# Revit family: STL23717_30 - 10°
name_source: partatom
category: Luminárias
units: mm (PartAtom-declared; Revit-internal decimal feet)

## family parameters
Com base no plano de trabalho = Não
Compartilhado = Não
Corte com vazios quando carregada = Não
Cota do conector redondo = Utilizar diâmetro
Fonte luminosa = Sim
Manter orientação da anotação = Não
Ponto de cálculo do ambiente = Não
Sempre na vertical = Sim
Tipo de parte = Normal

## types (1)
- STL23717/30 - BIVOLT - 3000K - 360lm - 14°
    Altura da Caixa de Instalação = 0.14 m
    Altura do Embutido = 0.1 m
    Arquivo de rede fotométrica = STELLA - STL23717-30 - EMBUTIDO DE SOLO GROUND 6W COM GRADE.ies
    Dimerização = Não dimerizável
    Diâmetro da Caixa de Instalação = 0.17 m
    Diâmetro do Embutido = 0.07 m
    Elevação padrão = 0 m
    Estrutura = Al - Preto
    Fabricante = Stella
    Filtro de cor = 16777215
    Fluxo Luminoso = 360 lm
    Grau de proteção (IP) = IP67
    IRC (Índice de reprodução de cores) = >80
    Luminoso = Luminoso - 3000K
    Modelo = S.Ground
    Potência = 7 W
    Referência = STL23717/30
    Temperatura da cor (K) = 3000 K
    Tensão Elétrica = 100V-240V
    Troca de temperatura da cor de lâmpada com esmaecimento = <Nenhum>
    URL = https://stella.com.br
    Vidro = Vidro
    Ângulo de Abertura = 14°
    Ângulo de inclinação = -90.00°
